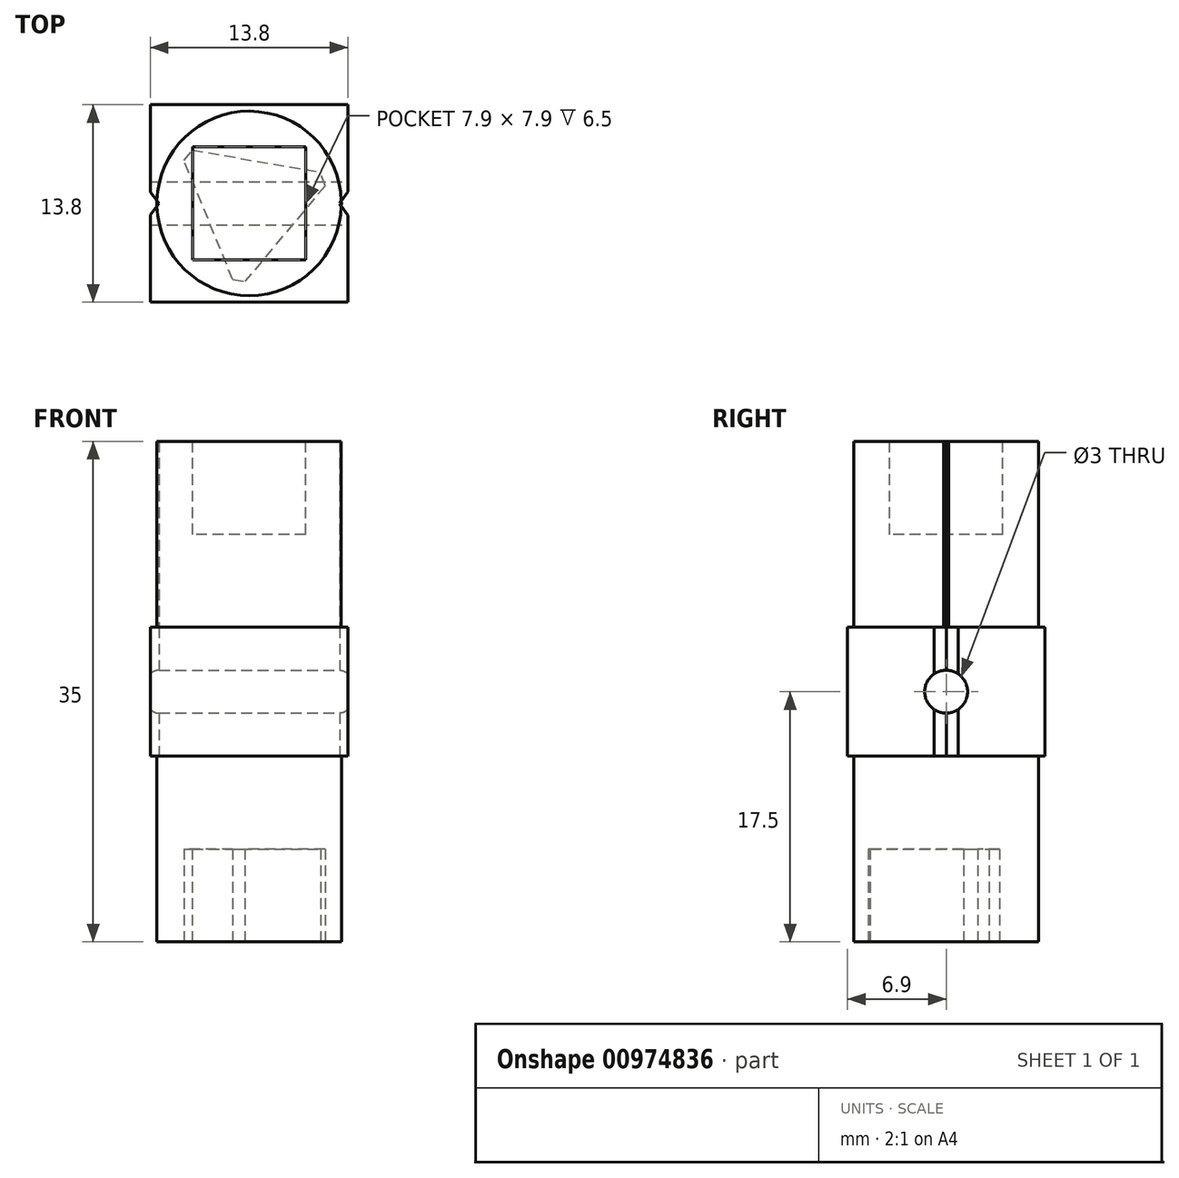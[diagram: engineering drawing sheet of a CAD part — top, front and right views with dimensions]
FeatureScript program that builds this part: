
annotation { "Feature Type Name" : "Feature", "Feature Type Description" : "" }
export const myFeature = defineFeature(function(context is Context, id is Id, definition is map)
    precondition{}
    {
        {
            var Q0;
            Q0=qCreatedBy(makeId("Top.planeOp"),FACE);
            var sketch = newSketch(context, id + "F0", { "sketchPlane" : qUnion([Q0])});
            skLineSegment(sketch, "E0.bottom", {"start": v(6.9, 6.9) * mm, "end": v(-6.9, 6.9) * mm});
            skLineSegment(sketch, "E0.top", {"start": v(6.9, -6.9) * mm, "end": v(-6.9, -6.9) * mm});
            skLineSegment(sketch, "E0.left", {"start": v(6.9, 6.9) * mm, "end": v(6.9, -6.9) * mm});
            skLineSegment(sketch, "E0.right", {"start": v(-6.9, 6.9) * mm, "end": v(-6.9, -6.9) * mm});
            skSolve(sketch);
        }
        {
            var Q0;
            Q0=qSketchRegion(id+"F0",true);
            extrude(context, id + "F1", {"entities" : qUnion([Q0]), "endBound" : BoundingType.SYMMETRIC, "depth" : 9 * mm, "offsetDistance" : 25 * mm});
        }
        {
            var Q0;
            Q0=makeQuery(id+"F1.opExtrude","CAP_FACE",FACE,{"disambiguationData":[OSD([sQuery(id+"F0.wireOp",EDGE,"E0.bottom"),sQuery(id+"F0.wireOp",EDGE,"E0.top"),sQuery(id+"F0.wireOp",EDGE,"E0.left"),sQuery(id+"F0.wireOp",EDGE,"E0.right")])],"isStart":false});
            var sketch = newSketch(context, id + "F2", { "sketchPlane" : qUnion([Q0])});
            skCircle(sketch, "E1", {"center": v(0, 0) * mm, "radius": 6.45 * mm});
            skSolve(sketch);
        }
        {
            var Q0;
            Q0=qSketchRegion(id+"F2",true);
            extrude(context, id + "F3", {"entities" : qUnion([Q0]), "depth" : 13 * mm, "offsetDistance" : 25 * mm});
        }
        {
            var Q0;
            Q0=makeQuery(id+"F1.opExtrude","CAP_FACE",FACE,{"disambiguationData":[OSD([sQuery(id+"F0.wireOp",EDGE,"E0.bottom"),sQuery(id+"F0.wireOp",EDGE,"E0.top"),sQuery(id+"F0.wireOp",EDGE,"E0.left"),sQuery(id+"F0.wireOp",EDGE,"E0.right")])],"isStart":true});
            var sketch = newSketch(context, id + "F4", { "sketchPlane" : qUnion([Q0])});
            skCircle(sketch, "E2", {"center": v(0, 0) * mm, "radius": 6.45 * mm});
            skSolve(sketch);
        }
        {
            var Q0;
            Q0=qSketchRegion(id+"F4",true);
            extrude(context, id + "F5", {"entities" : qUnion([Q0]), "depth" : 13 * mm, "offsetDistance" : 25 * mm});
        }
        {
            var Q0;
            Q0=makeQuery(id+"F1.opExtrude","SWEPT_FACE",FACE,{"disambiguationData":[OSD([sQuery(id+"F0.wireOp",EDGE,"E0.left")])]});
            var sketch = newSketch(context, id + "F6", { "sketchPlane" : qUnion([Q0])});
            skCircle(sketch, "E3", {"center": v(0, 0) * mm, "radius": 1.5 * mm});
            skSolve(sketch);
        }
        {
            var Q0;
            Q0=qSketchRegion(id+"F6",true);
            extrude(context, id + "F7", {"entities" : qUnion([Q0]), "operationType" : NewBodyOperationType.REMOVE, "endBound" : BoundingType.THROUGH_ALL, "oppositeDirection" : true, "depth" : 25 * mm, "offsetDistance" : 25 * mm});
        }
        {
            var Q0;
            Q0=makeQuery(id+"F1.opExtrude","CAP_FACE",FACE,{"disambiguationData":[OSD([sQuery(id+"F0.wireOp",EDGE,"E0.bottom"),sQuery(id+"F0.wireOp",EDGE,"E0.top"),sQuery(id+"F0.wireOp",EDGE,"E0.left"),sQuery(id+"F0.wireOp",EDGE,"E0.right")])],"isStart":true});
            var sketch = newSketch(context, id + "F8", { "sketchPlane" : qUnion([Q0])});
            skLineSegment(sketch, "E4", {"start": v(6.34, 0) * mm, "end": v(6.9, 0.83) * mm});
            skLineSegment(sketch, "E5", {"start": v(6.34, 0) * mm, "end": v(6.9, -0.83) * mm});
            skLineSegment(sketch, "E6", {"start": v(6.9, 0.83) * mm, "end": v(6.9, -0.83) * mm});
            skLineSegment(sketch, "E7", {"start": v(-6.3, 0) * mm, "end": v(-6.9, 0.8) * mm});
            skLineSegment(sketch, "E8", {"start": v(-6.3, 0) * mm, "end": v(-6.9, -0.8) * mm});
            skLineSegment(sketch, "E9", {"start": v(-6.9, -0.8) * mm, "end": v(-6.9, 0.8) * mm});
            skSolve(sketch);
        }
        {
            var Q0;
            Q0=qSketchRegion(id+"F8",true);
            extrude(context, id + "F9", {"entities" : qUnion([Q0]), "operationType" : NewBodyOperationType.REMOVE, "endBound" : BoundingType.THROUGH_ALL, "oppositeDirection" : true, "depth" : 25 * mm, "offsetDistance" : 25 * mm});
        }
        {
            var Q0;
            Q0=makeQuery(id+"F3.opExtrude","CAP_FACE",FACE,{"disambiguationData":[OSD([sQuery(id+"F2.wireOp",EDGE,"E1")])],"isStart":false});
            var sketch = newSketch(context, id + "F10", { "sketchPlane" : qUnion([Q0])});
            skLineSegment(sketch, "E10.bottom", {"start": v(3.95, 3.95) * mm, "end": v(-3.95, 3.95) * mm});
            skLineSegment(sketch, "E10.top", {"start": v(3.95, -3.95) * mm, "end": v(-3.95, -3.95) * mm});
            skLineSegment(sketch, "E10.left", {"start": v(3.95, 3.95) * mm, "end": v(3.95, -3.95) * mm});
            skLineSegment(sketch, "E10.right", {"start": v(-3.95, 3.95) * mm, "end": v(-3.95, -3.95) * mm});
            skSolve(sketch);
        }
        {
            var Q0;
            Q0=qSketchRegion(id+"F10",true);
            extrude(context, id + "F11", {"entities" : qUnion([Q0]), "operationType" : NewBodyOperationType.REMOVE, "oppositeDirection" : true, "depth" : 6.5 * mm, "offsetDistance" : 25 * mm});
        }
        {
            var Q0;
            Q0=makeQuery(id+"F5.opExtrude","CAP_FACE",FACE,{"disambiguationData":[OSD([sQuery(id+"F4.wireOp",EDGE,"E2")])],"isStart":false});
            var sketch = newSketch(context, id + "F12", { "sketchPlane" : qUnion([Q0])});
            skCircle(sketch, "E11.0", {"center": v(0, 0) * mm, "radius": 5.45 * mm});
            skLineSegment(sketch, "E12", {"start": v(-1.14, 5.33) * mm, "end": v(-4.55, -3) * mm});
            skLineSegment(sketch, "E13", {"start": v(-3.98, -3.72) * mm, "end": v(5, -2.2) * mm});
            skLineSegment(sketch, "E14", {"start": v(5.31, -1.22) * mm, "end": v(-0.28, 5.44) * mm});
            skLineSegment(sketch, "E15", {"start": v(-1.14, 5.33) * mm, "end": v(-0.28, 5.44) * mm});
            skLineSegment(sketch, "E16", {"start": v(5.31, -1.22) * mm, "end": v(5, -2.2) * mm});
            skLineSegment(sketch, "E17", {"start": v(-4.55, -3) * mm, "end": v(-3.98, -3.72) * mm});
            skSolve(sketch);
        }
        {
            var Q0;
            Q0=makeQuery(id+"F12.imprint","IMPRINT",FACE,{"disambiguationData":[TD([[makeQuery(id+"F12.imprint","IMPRINT",EDGE,{"derivedFrom":sQuery(id+"F12.wireOp",EDGE,"E12")}),1.0]])]});
            extrude(context, id + "F13", {"entities" : qUnion([Q0]), "operationType" : NewBodyOperationType.REMOVE, "oppositeDirection" : true, "depth" : 6.5 * mm, "offsetDistance" : 25 * mm});
        }
    });
